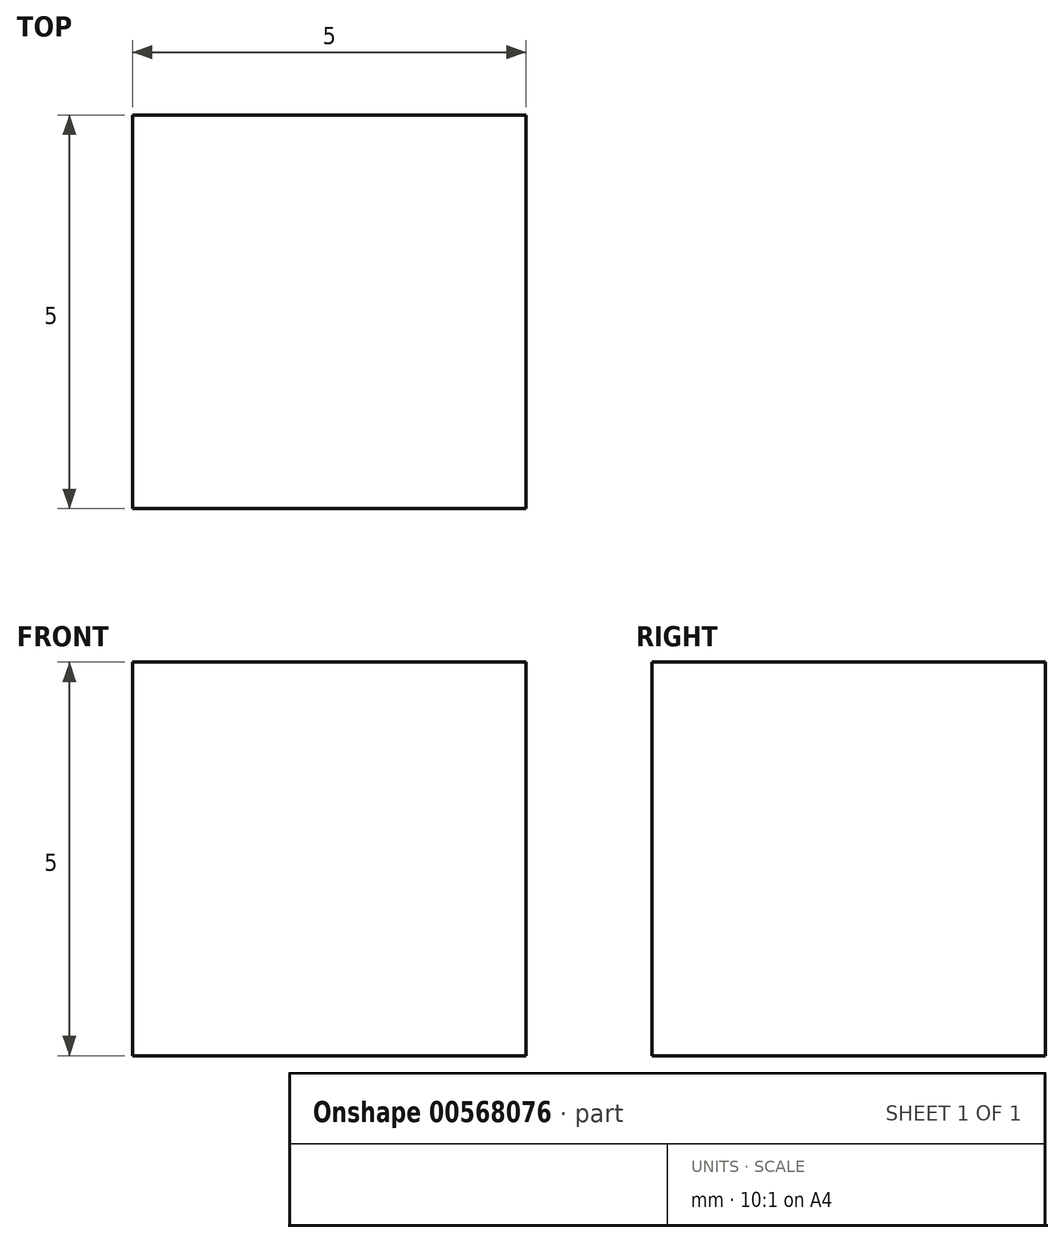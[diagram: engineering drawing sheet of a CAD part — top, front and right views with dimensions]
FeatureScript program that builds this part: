
annotation { "Feature Type Name" : "Feature", "Feature Type Description" : "" }
export const myFeature = defineFeature(function(context is Context, id is Id, definition is map)
    precondition{}
    {
        {
            var Q0;
            Q0=qCreatedBy(makeId("Top.planeOp"),FACE);
            var sketch = newSketch(context, id + "F0", { "sketchPlane" : qUnion([Q0])});
            skLineSegment(sketch, "E0.bottom", {"start": v(-43.23, 19.57) * mm, "end": v(-38.23, 19.57) * mm});
            skLineSegment(sketch, "E0.top", {"start": v(-43.23, 14.57) * mm, "end": v(-38.23, 14.57) * mm});
            skLineSegment(sketch, "E0.left", {"start": v(-43.23, 19.57) * mm, "end": v(-43.23, 14.57) * mm});
            skLineSegment(sketch, "E0.right", {"start": v(-38.23, 19.57) * mm, "end": v(-38.23, 14.57) * mm});
            skSolve(sketch);
        }
        {
            var Q0;
            Q0=makeQuery(id+"F0.imprint","IMPRINT",FACE,{"disambiguationData":[TD([[makeQuery(id+"F0.imprint","IMPRINT",EDGE,{"derivedFrom":sQuery(id+"F0.wireOp",EDGE,"E0.bottom")}),-1.0]])]});
            extrude(context, id + "F1", {"entities" : qUnion([Q0]), "depth" : 5 * mm, "offsetDistance" : 25 * mm});
        }
    });
